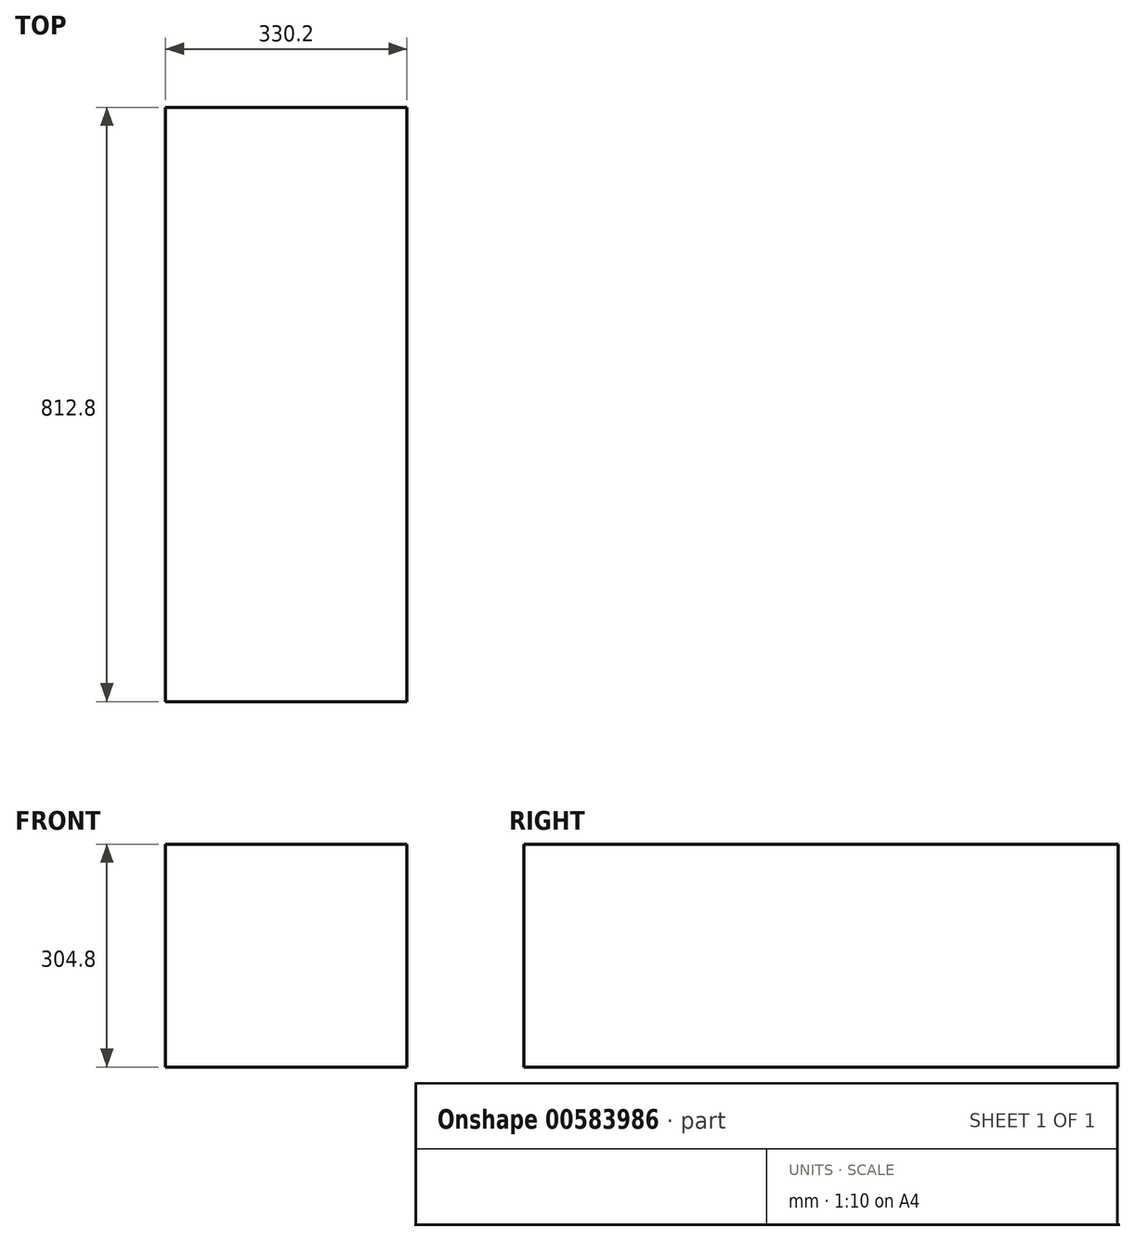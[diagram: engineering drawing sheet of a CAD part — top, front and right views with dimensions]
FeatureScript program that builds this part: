
annotation { "Feature Type Name" : "Feature", "Feature Type Description" : "" }
export const myFeature = defineFeature(function(context is Context, id is Id, definition is map)
    precondition{}
    {
        {
            var Q0;
            Q0=qCreatedBy(makeId("Top.planeOp"),FACE);
            var sketch = newSketch(context, id + "F0", { "sketchPlane" : qUnion([Q0])});
            skLineSegment(sketch, "E0.bottom", {"start": v(-125.92, 650.99) * mm, "end": v(204.28, 650.99) * mm});
            skLineSegment(sketch, "E0.top", {"start": v(-125.92, -161.81) * mm, "end": v(204.28, -161.81) * mm});
            skLineSegment(sketch, "E0.left", {"start": v(-125.92, 650.99) * mm, "end": v(-125.92, -161.81) * mm});
            skLineSegment(sketch, "E0.right", {"start": v(204.28, 650.99) * mm, "end": v(204.28, -161.81) * mm});
            skSolve(sketch);
        }
        {
            var Q0;
            Q0=makeQuery(id+"F0.imprint","IMPRINT",FACE,{"disambiguationData":[TD([[makeQuery(id+"F0.imprint","IMPRINT",EDGE,{"derivedFrom":sQuery(id+"F0.wireOp",EDGE,"E0.bottom")}),-1.0]])]});
            extrude(context, id + "F1", {"entities" : qUnion([Q0]), "depth" : 304.8 * mm, "offsetDistance" : 25.4 * mm});
        }
    });
